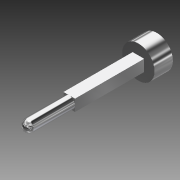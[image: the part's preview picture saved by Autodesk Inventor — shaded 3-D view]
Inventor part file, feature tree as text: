
AUTODESK INVENTOR PART (.ipt)
format: ipt  version: 2013 (Build 170138000, 138)  size: 94,720 bytes
history: native  units: in
note: dims shown in document units (in); Inventor stores cm internally (conversion verified against a paired STEP export)
features: sketch x2, revolve x1, extrude x1
ambient origin geometry x8: Origin, YZ Plane, XZ Plane, XY Plane, X Axis, Y Axis, Z Axis, Center Point
feature tree (4):
  revolve  "Revolution2"  [1 undecoded]
  extrude  "Extrusion1"  Depth=0.1575in
  sketch  "Sketch2"  dims[d13=1.1417in d15=0.0492in]
  sketch  "Sketch3"  dims[d16=0.1378in d17=0.1575in d18=90.0deg d19=0.5906in d20=0.0in]
note: 1 required parameter value undecoded (feature->parameter linkage not recoverable at this tier; creation-order binding heuristic only, values carry confidence <= 0.55)
